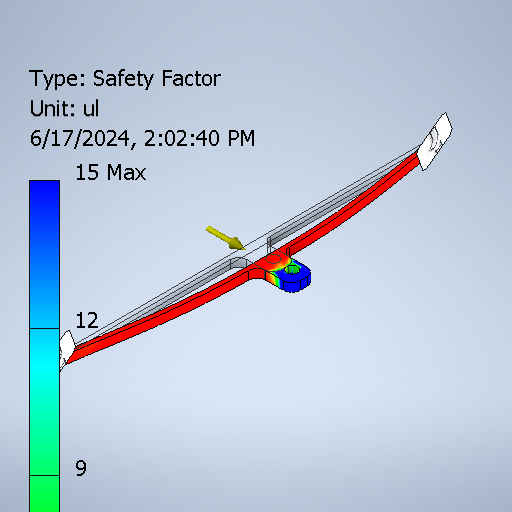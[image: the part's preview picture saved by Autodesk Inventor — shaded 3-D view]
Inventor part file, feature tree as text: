
AUTODESK INVENTOR PART (.ipt)
format: ipt  version: 2025 (Build 290162010, 162A)  size: 315,904 bytes
history: native  units: mm
features: sketch x2, extrude x1, hole x1, fillet x1
ambient origin geometry x8: Origin, YZ Plane, XZ Plane, XY Plane, X Axis, Y Axis, Z Axis, Center Point
bodies: Solid1 (feature_tree)
feature tree (5):
  extrude  "Extrusion1"  Depth=90.0mm
  hole  "Hole1"  [1 undecoded]
  fillet  "Fillet1"  Radius=5.0mm
  sketch  "Sketch1"  dims[d0=1.0mm d1=90.0mm]
  sketch  "Sketch3"  dims[d2=30.0mm d3=2.0mm d4=0.0mm d5=5.0mm d6=2.6416mm d7=7.01mm d8=4.0mm d9=2.0mm d10=90.0deg d11=10.979mm d12=0.0mm d13=44.5mm d14=2.0mm]
note: 1 required parameter value undecoded (feature->parameter linkage not recoverable at this tier; creation-order binding heuristic only, values carry confidence <= 0.55)
